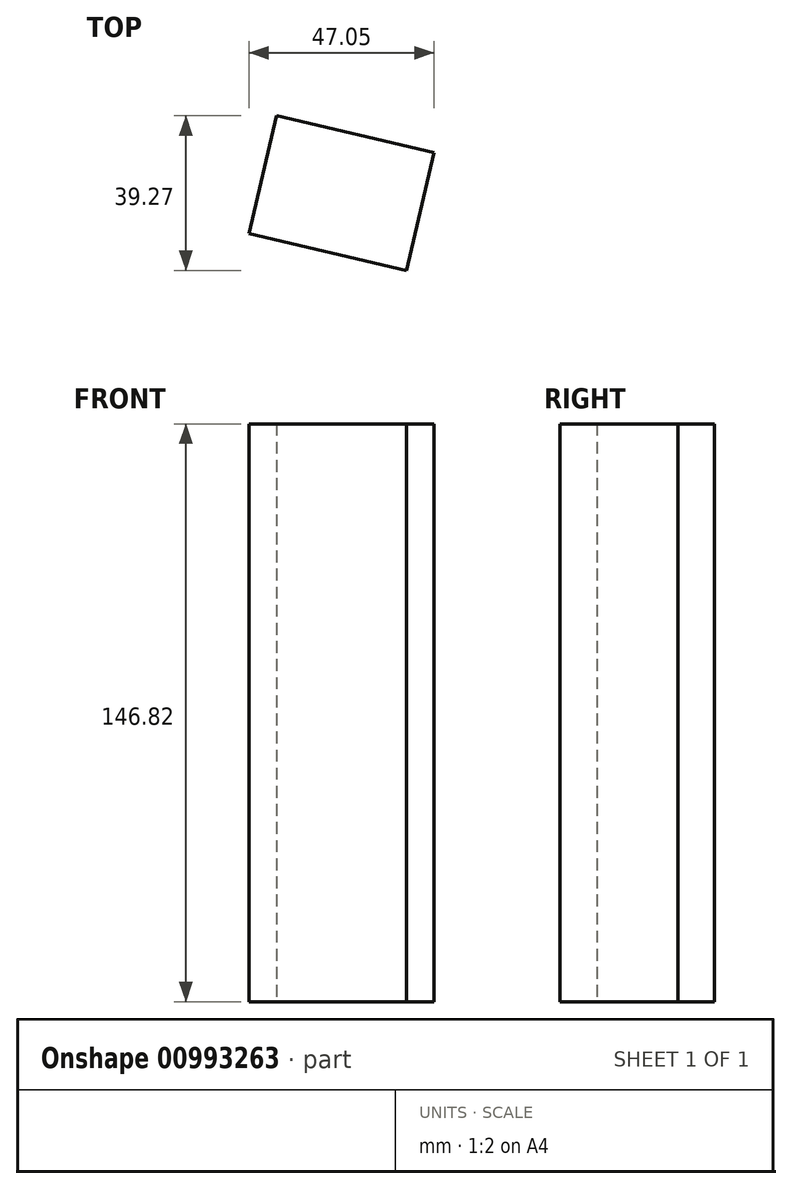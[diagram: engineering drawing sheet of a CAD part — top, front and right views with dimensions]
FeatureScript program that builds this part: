
annotation { "Feature Type Name" : "Feature", "Feature Type Description" : "" }
export const myFeature = defineFeature(function(context is Context, id is Id, definition is map)
    precondition{}
    {
        {
            var Q0;
            Q0=qCreatedBy(makeId("Top.planeOp"),FACE);
            var sketch = newSketch(context, id + "F0", { "sketchPlane" : qUnion([Q0])});
            skLineSegment(sketch, "E0.bottom", {"start": v(-15.1, 20.64) * mm, "end": v(15.64, 20.64) * mm});
            skLineSegment(sketch, "E0.top", {"start": v(-15.1, -20.5) * mm, "end": v(15.64, -20.5) * mm});
            skLineSegment(sketch, "E0.left", {"start": v(-15.1, 20.64) * mm, "end": v(-15.1, -20.5) * mm});
            skLineSegment(sketch, "E0.right", {"start": v(15.64, 20.64) * mm, "end": v(15.64, -20.5) * mm});
            skSolve(sketch);
        }
        {
            var Q0;
            Q0=makeQuery(id+"F0.imprint","IMPRINT",FACE,{"disambiguationData":[TD([[makeQuery(id+"F0.imprint","IMPRINT",EDGE,{"derivedFrom":sQuery(id+"F0.wireOp",EDGE,"E0.bottom")}),-1.0]])]});
            extrude(context, id + "F1", {"entities" : qUnion([Q0]), "depth" : 146.82 * mm, "offsetDistance" : 25.4 * mm});
        }
        {
            var Q0;
            Q0=makeQuery(id+"F1.opExtrude","SWEPT_BODY",BODY,{"disambiguationData":[OSD([sQuery(id+"F0.wireOp",EDGE,"E0.bottom"),sQuery(id+"F0.wireOp",EDGE,"E0.top"),sQuery(id+"F0.wireOp",EDGE,"E0.left"),sQuery(id+"F0.wireOp",EDGE,"E0.right")])]});
            var Q1;
            Q1=makeQuery(id+"F1.opExtrude","SWEPT_EDGE",EDGE,{"disambiguationData":[OSD([sQuery(id+"F0.wireOp",EDGE,"E0.top"),sQuery(id+"F0.wireOp",EDGE,"E0.right")])]});
            transform(context, id + "F2", {"entities" : qUnion([Q0]), "transformType" : TransformType.ROTATION, "transformAxis" : qUnion([Q1]), "angle" : 103.13 * degree, "makeCopy" : false});
        }
    });
